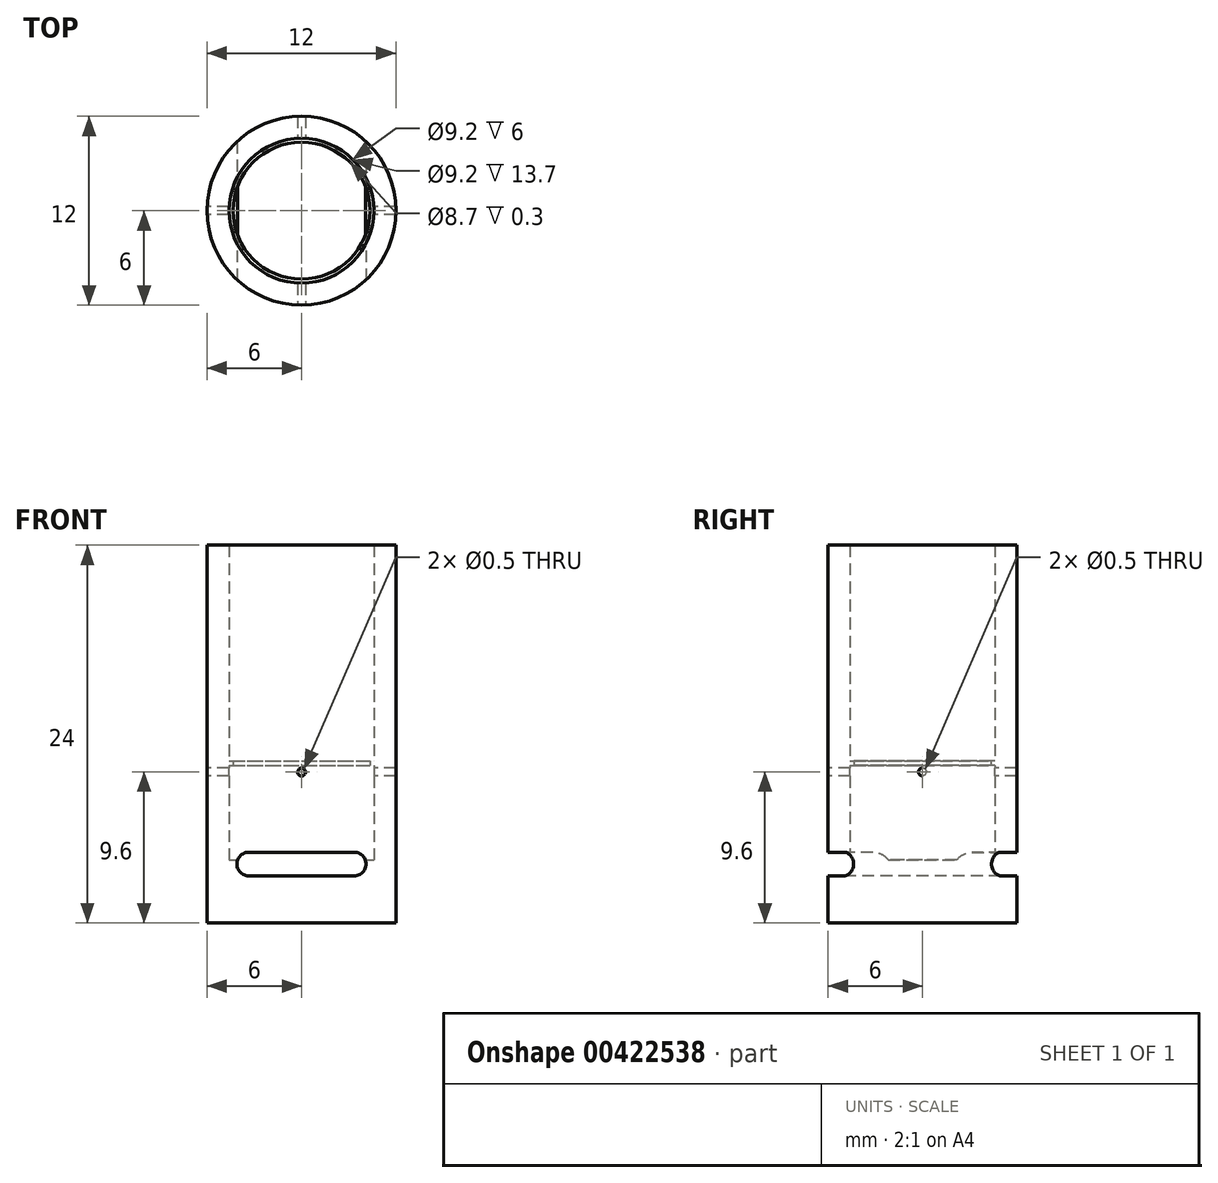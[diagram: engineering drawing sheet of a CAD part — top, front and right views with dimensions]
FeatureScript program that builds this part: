
annotation { "Feature Type Name" : "Feature", "Feature Type Description" : "" }
export const myFeature = defineFeature(function(context is Context, id is Id, definition is map)
    precondition{}
    {
        {
            var Q0;
            Q0=qCreatedBy(makeId("Top.planeOp"),FACE);
            var sketch = newSketch(context, id + "F0", { "sketchPlane" : qUnion([Q0])});
            skCircle(sketch, "E0", {"center": v(0, 0) * mm, "radius": 6 * mm});
            skSolve(sketch);
        }
        {
            var Q0;
            Q0=qSketchRegion(id+"F0",true);
            extrude(context, id + "F1", {"entities" : qUnion([Q0]), "offsetDistance" : 25 * mm, "depth" : 4 * mm});
        }
        {
            var Q0;
            Q0=makeQuery(id+"F1.opExtrude","CAP_FACE",FACE,{"disambiguationData":[OSD([sQuery(id+"F0.wireOp",EDGE,"E0")])],"isStart":false});
            var sketch = newSketch(context, id + "F2", { "sketchPlane" : qUnion([Q0])});
            skCircle(sketch, "E1", {"center": v(0, 0) * mm, "radius": 4.6 * mm});
            skSolve(sketch);
        }
        {
            var Q0;
            Q0=makeQuery(id+"F2.imprint","IMPRINT",FACE,{"disambiguationData":[TD([[makeQuery(id+"F2.imprint","IMPRINT",EDGE,{"derivedFrom":sQuery(id+"F2.wireOp",EDGE,"E1")}),-1.0]])]});
            extrude(context, id + "F3", {"entities" : qUnion([Q0]), "operationType" : NewBodyOperationType.ADD, "offsetDistance" : 25 * mm, "depth" : 20 * mm});
        }
        {
            var Q0;
            Q0=qCreatedBy(makeId("Front.planeOp"),FACE);
            cPlane(context, id + "F4", {"entities" : qUnion([Q0]), "cplaneType" : CPlaneType.OFFSET, "offset" : 10 * mm, "width" : 150 * mm, "height" : 150 * mm});
        }
        {
            var Q0;
            Q0=qCreatedBy(id+"F4.planeOp",FACE);
            var sketch = newSketch(context, id + "F5", { "sketchPlane" : qUnion([Q0])});
            skLineSegment(sketch, "E2.bottom", {"start": v(-3.35, 4.5) * mm, "end": v(3.35, 4.5) * mm});
            skLineSegment(sketch, "E2.top", {"start": v(-3.35, 3) * mm, "end": v(3.35, 3) * mm});
            skLineSegment(sketch, "E2.left", {"start": v(-3.35, 4.5) * mm, "end": v(-3.35, 3) * mm});
            skLineSegment(sketch, "E2.right", {"start": v(3.35, 4.5) * mm, "end": v(3.35, 3) * mm});
            skLineSegment(sketch, "E3", {"start": v(0, 0) * mm, "end": v(0, 11.71) * mm, "construction": true});
            skPoint(sketch, "E4", {"position": v(0, 3) * mm});
            skCircle(sketch, "E5", {"center": v(3.35, 3.75) * mm, "radius": 0.75 * mm});
            skCircle(sketch, "E6", {"center": v(-3.35, 3.75) * mm, "radius": 0.75 * mm});
            skSolve(sketch);
        }
        {
            var Q0;
            Q0=qSketchRegion(id+"F5",true);
            extrude(context, id + "F6", {"entities" : qUnion([Q0]), "operationType" : NewBodyOperationType.REMOVE, "oppositeDirection" : true, "depth" : 25 * mm});
        }
        {
            var Q0;
            Q0=makeQuery(id+"F1.opExtrude","CAP_FACE",FACE,{"disambiguationData":[OSD([sQuery(id+"F0.wireOp",EDGE,"E0")])],"isStart":true});
            cPlane(context, id + "F7", {"entities" : qUnion([Q0]), "cplaneType" : CPlaneType.OFFSET, "offset" : 10 * mm, "oppositeDirection" : true, "width" : 150 * mm, "height" : 150 * mm});
        }
        {
            var Q0;
            Q0=qCreatedBy(id+"F7.planeOp",FACE);
            var sketch = newSketch(context, id + "F8", { "sketchPlane" : qUnion([Q0])});
            skCircle(sketch, "E7", {"center": v(0, 0) * mm, "radius": 4.35 * mm});
            skCircle(sketch, "E8", {"center": v(0, 0) * mm, "radius": 4.6 * mm});
            skSolve(sketch);
        }
        {
            var Q0;
            Q0 = qSketchRegion(id + "F8", true);
            extrude(context, id + "F9", {"entities" : qUnion([Q0]), "operationType" : NewBodyOperationType.ADD, "oppositeDirection" : true, "depth" : 0.3 * mm});
        }
        {
            var Q0;
            Q0=qCreatedBy(id+"F4.planeOp",FACE);
            var sketch = newSketch(context, id + "F10", { "sketchPlane" : qUnion([Q0])});
            skCircle(sketch, "E9", {"center": v(0, 9.6) * mm, "radius": 0.25 * mm});
            skSolve(sketch);
        }
        {
            var Q0;
            Q0=makeQuery(id+"F10.imprint","IMPRINT",FACE,{"disambiguationData":[TD([[makeQuery(id+"F10.imprint","IMPRINT",EDGE,{"derivedFrom":sQuery(id+"F10.wireOp",EDGE,"E9")}),1.0]])]});
            var Q1;
            Q1=sQuery(id+"F10.wireOp",EDGE,"E9");
            extrude(context, id + "F11", {"entities" : qUnion([Q0]), "operationType" : NewBodyOperationType.REMOVE, "surfaceEntities" : qUnion([Q1]), "oppositeDirection" : true, "depth" : 25 * mm});
        }
        {
            var Q0;
            Q0=qCreatedBy(makeId("Right.planeOp"),FACE);
            cPlane(context, id + "F12", {"entities" : qUnion([Q0]), "cplaneType" : CPlaneType.OFFSET, "offset" : 15 * mm, "oppositeDirection" : true, "width" : 150 * mm, "height" : 150 * mm});
        }
        {
            var Q0;
            Q0=qCreatedBy(id+"F12.planeOp",FACE);
            var sketch = newSketch(context, id + "F13", { "sketchPlane" : qUnion([Q0])});
            skCircle(sketch, "E10", {"center": v(0, 9.6) * mm, "radius": 0.25 * mm});
            skSolve(sketch);
        }
        {
            var Q0;
            Q0=makeQuery(id+"F13.imprint","IMPRINT",FACE,{"disambiguationData":[TD([[makeQuery(id+"F13.imprint","IMPRINT",EDGE,{"derivedFrom":sQuery(id+"F13.wireOp",EDGE,"E10")}),1.0]])]});
            var Q1;
            Q1=sQuery(id+"F13.wireOp",EDGE,"E10");
            extrude(context, id + "F14", {"entities" : qUnion([Q0]), "operationType" : NewBodyOperationType.REMOVE, "surfaceEntities" : qUnion([Q1]), "depth" : 25 * mm});
        }
    });
